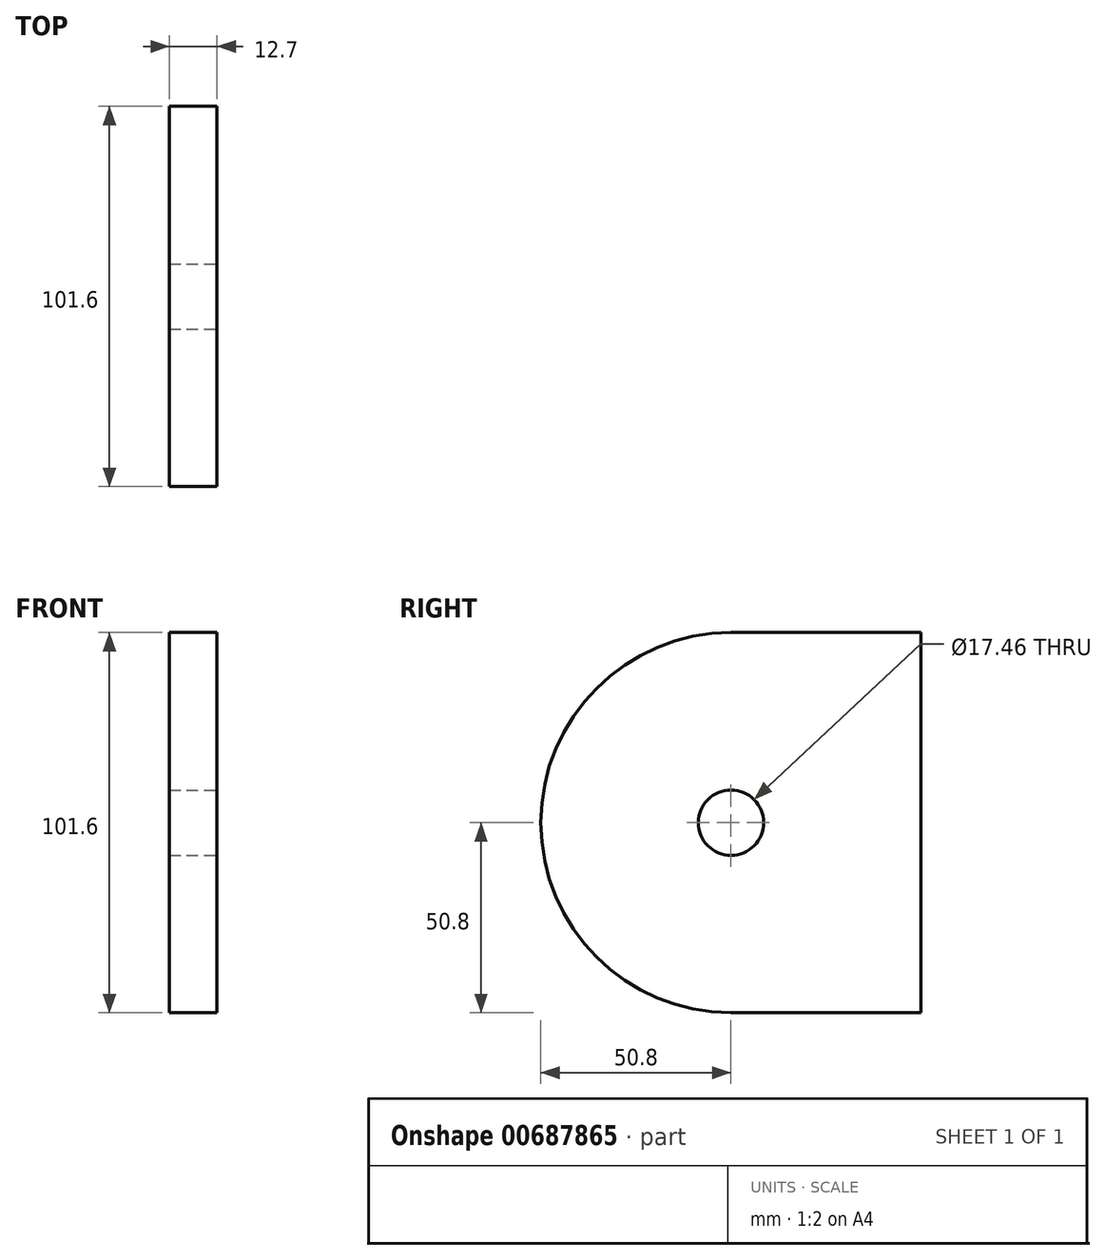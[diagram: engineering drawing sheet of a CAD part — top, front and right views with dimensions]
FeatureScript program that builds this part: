
annotation { "Feature Type Name" : "Feature", "Feature Type Description" : "" }
export const myFeature = defineFeature(function(context is Context, id is Id, definition is map)
    precondition{}
    {
        {
            var Q0;
            Q0=qCreatedBy(makeId("Right.planeOp"),FACE);
            var sketch = newSketch(context, id + "F0", { "sketchPlane" : qUnion([Q0])});
            skLineSegment(sketch, "E0.bottom", {"start": v(0, 0) * mm, "end": v(-101.6, 0) * mm});
            skLineSegment(sketch, "E0.top", {"start": v(0, 101.6) * mm, "end": v(-101.6, 101.6) * mm});
            skLineSegment(sketch, "E0.left", {"start": v(0, 0) * mm, "end": v(0, 101.6) * mm});
            skLineSegment(sketch, "E0.right", {"start": v(-101.6, 0) * mm, "end": v(-101.6, 101.6) * mm});
            skSolve(sketch);
        }
        {
            var Q0;
            Q0=makeQuery(id+"F0.imprint","IMPRINT",FACE,{"disambiguationData":[TD([[makeQuery(id+"F0.imprint","IMPRINT",EDGE,{"derivedFrom":sQuery(id+"F0.wireOp",EDGE,"E0.bottom")}),-1.0]])]});
            extrude(context, id + "F1", {"entities" : qUnion([Q0]), "endBound" : BoundingType.SYMMETRIC, "depth" : 12.7 * mm, "offsetDistance" : 25.4 * mm});
        }
        {
            var Q0;
            Q0=makeQuery(id+"F1.opExtrude","SWEPT_EDGE",EDGE,{"disambiguationData":[OSD([sQuery(id+"F0.wireOp",EDGE,"E0.top"),sQuery(id+"F0.wireOp",EDGE,"E0.right")])]});
            var Q1;
            Q1=makeQuery(id+"F1.opExtrude","SWEPT_EDGE",EDGE,{"disambiguationData":[OSD([sQuery(id+"F0.wireOp",EDGE,"E0.bottom"),sQuery(id+"F0.wireOp",EDGE,"E0.right")])]});
            fillet(context, id + "F2", {"entities" : qUnion([Q0, Q1]), "radius" : 50.8 * mm, "tangentPropagation" : true, "allowEdgeOverflow" : false});
        }
        {
            var Q0;
            Q0=makeQuery(id+"F1.opExtrude","CAP_FACE",FACE,{"disambiguationData":[OSD([sQuery(id+"F0.wireOp",EDGE,"E0.bottom"),sQuery(id+"F0.wireOp",EDGE,"E0.top"),sQuery(id+"F0.wireOp",EDGE,"E0.left"),sQuery(id+"F0.wireOp",EDGE,"E0.right")])],"isStart":false});
            var sketch = newSketch(context, id + "F3", { "sketchPlane" : qUnion([Q0])});
            skCircle(sketch, "E1", {"center": v(-50.8, 50.8) * mm, "radius": 8.73 * mm});
            skSolve(sketch);
        }
        {
            var Q0;
            Q0=makeQuery(id+"F3.imprint","IMPRINT",FACE,{"disambiguationData":[TD([[makeQuery(id+"F3.imprint","IMPRINT",EDGE,{"derivedFrom":sQuery(id+"F3.wireOp",EDGE,"E1")}),1.0]])]});
            extrude(context, id + "F4", {"entities" : qUnion([Q0]), "operationType" : NewBodyOperationType.REMOVE, "oppositeDirection" : true, "depth" : 25.4 * mm, "offsetDistance" : 25.4 * mm});
        }
    });
